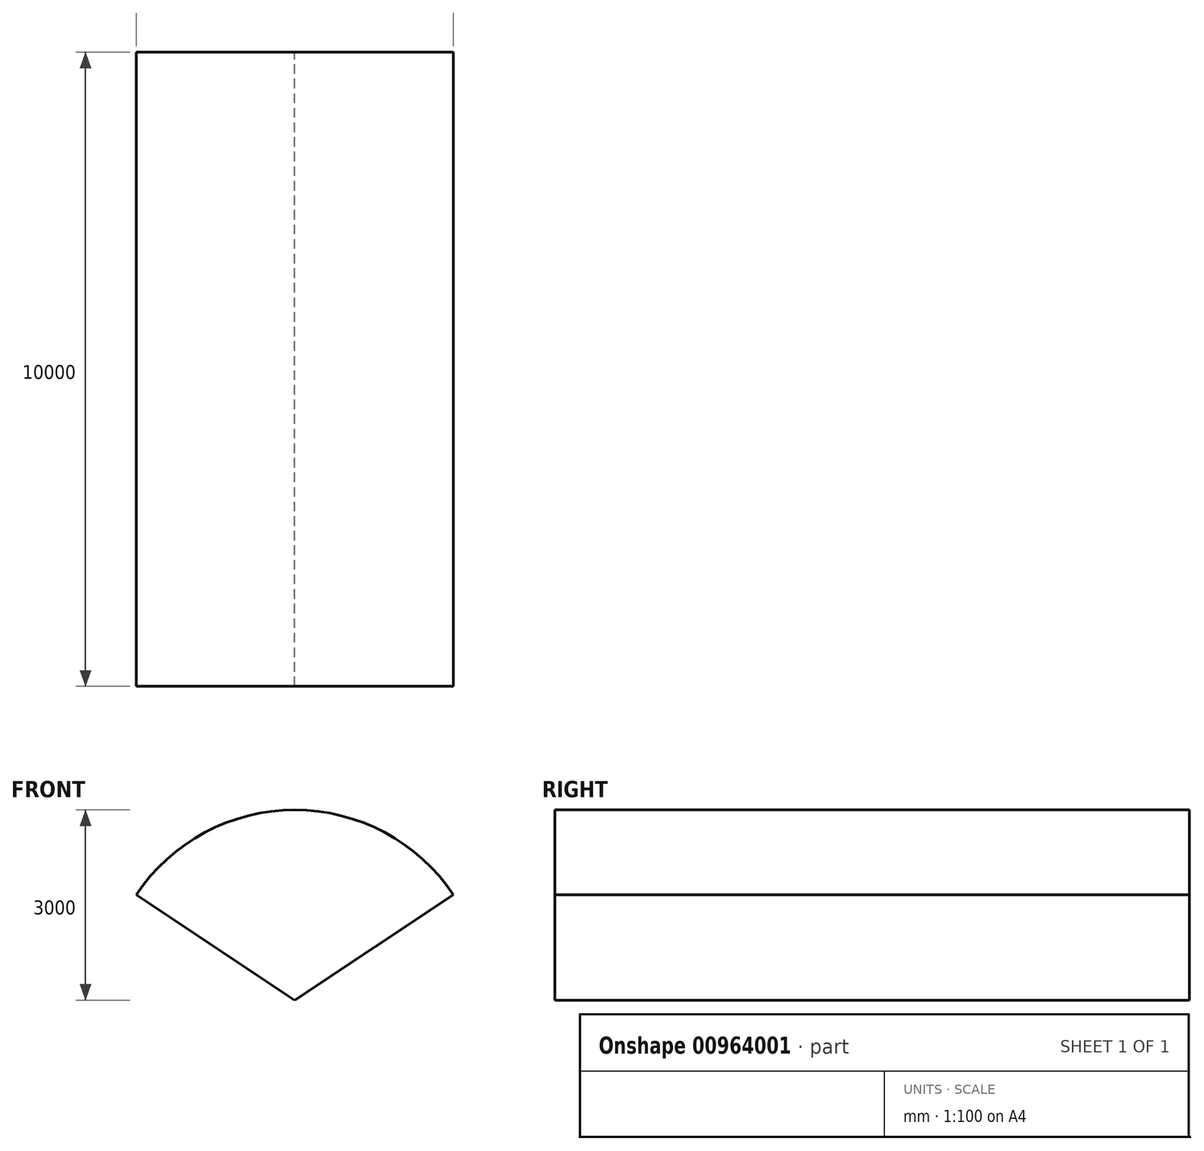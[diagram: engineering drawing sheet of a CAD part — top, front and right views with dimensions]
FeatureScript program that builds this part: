
annotation { "Feature Type Name" : "Feature", "Feature Type Description" : "" }
export const myFeature = defineFeature(function(context is Context, id is Id, definition is map)
    precondition{}
    {
        {
            var Q0;
            Q0=qCreatedBy(makeId("Front.planeOp"),FACE);
            var sketch = newSketch(context, id + "F0", { "sketchPlane" : qUnion([Q0])});
            skArc(sketch, "E0", {"start": v(2496.38, 0) * mm, "mid": v(-3.62, 1341.69) * mm, "end": v(-2503.62, 0) * mm});
            skLineSegment(sketch, "E1", {"start": v(-3.62, 1341.69) * mm, "end": v(-3.62, -1658.31) * mm});
            skLineSegment(sketch, "E2", {"start": v(-3.62, -1658.31) * mm, "end": v(-2503.62, 0) * mm});
            skLineSegment(sketch, "E3", {"start": v(2496.38, 0) * mm, "end": v(-3.62, -1658.31) * mm});
            skSolve(sketch);
        }
        {
            var Q0;
            {var subQ2=sQuery(id+"F0.wireOp",EDGE,"E1");Q0=makeQuery(id+"F0.imprint","IMPRINT",FACE,{"disambiguationData":[TD([[makeQuery(id+"F0.imprint","IMPRINT",EDGE,{"derivedFrom":subQ2}),-1.0]])]});}
            var Q1;
            Q1 = qSketchRegion(id + "F0", true);
            extrude(context, id + "F1", {"entities" : qUnion([Q0, Q1]), "depth" : 10000 * mm, "offsetDistance" : 25.4 * mm});
        }
    });
